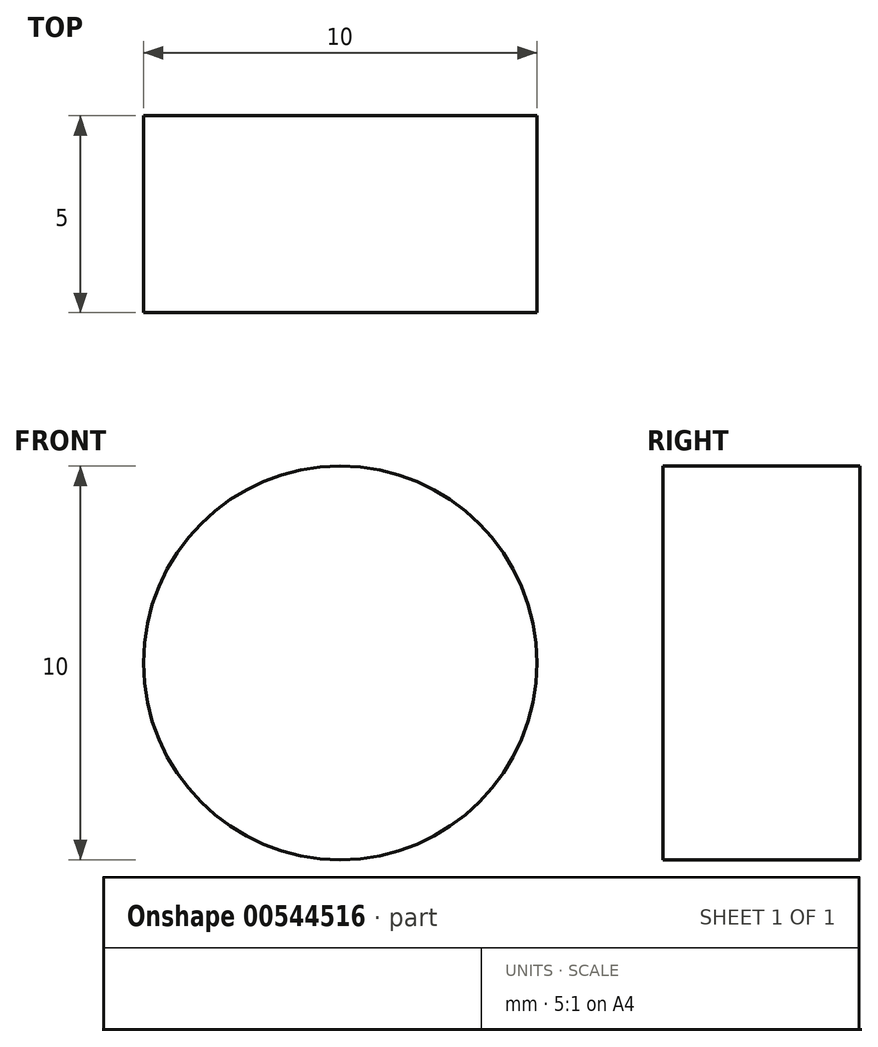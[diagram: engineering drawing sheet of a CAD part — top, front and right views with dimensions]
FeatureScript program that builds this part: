
annotation { "Feature Type Name" : "Feature", "Feature Type Description" : "" }
export const myFeature = defineFeature(function(context is Context, id is Id, definition is map)
    precondition{}
    {
        {
            var Q0;
            Q0=qCreatedBy(makeId("Front.planeOp"),FACE);
            var sketch = newSketch(context, id + "F0", { "sketchPlane" : qUnion([Q0])});
            skLineSegment(sketch, "E0", {"start": v(0, 0) * mm, "end": v(150, 0) * mm});
            skLineSegment(sketch, "E1", {"start": v(150, 0) * mm, "end": v(150, 40) * mm});
            skLineSegment(sketch, "E2", {"start": v(150, 40) * mm, "end": v(0, 40) * mm});
            skLineSegment(sketch, "E3", {"start": v(0, 40) * mm, "end": v(0, 0) * mm});
            skSolve(sketch);
        }
        {
            var Q0;
            Q0=makeQuery(id+"F0.imprint","IMPRINT",FACE,{"disambiguationData":[TD([[makeQuery(id+"F0.imprint","IMPRINT",EDGE,{"derivedFrom":sQuery(id+"F0.wireOp",EDGE,"E0")}),1.0]])]});
            extrude(context, id + "F1", {"entities" : qUnion([Q0]), "depth" : 5 * mm, "offsetDistance" : 25 * mm});
        }
        {
            var Q0;
            Q0=makeQuery(id+"F1.opExtrude","CAP_FACE",FACE,{"disambiguationData":[OSD([sQuery(id+"F0.wireOp",EDGE,"E0"),sQuery(id+"F0.wireOp",EDGE,"E1"),sQuery(id+"F0.wireOp",EDGE,"E2"),sQuery(id+"F0.wireOp",EDGE,"E3")])],"isStart":false});
            var sketch = newSketch(context, id + "F2", { "sketchPlane" : qUnion([Q0])});
            skLineSegment(sketch, "E4", {"start": v(0, 20) * mm, "end": v(15, 20) * mm, "construction": true});
            skPoint(sketch, "E4.endSnap0", {"position": v(0, 20) * mm});
            skLineSegment(sketch, "E5", {"start": v(75, 0) * mm, "end": v(75, 40) * mm, "construction": true});
            skCircle(sketch, "E6", {"center": v(15, 20) * mm, "radius": 5 * mm});
            skCircle(sketch, "E7.MirrorC", {"center": v(135, 20) * mm, "radius": 5 * mm});
            skSolve(sketch);
        }
        {
            var Q0;
            Q0=makeQuery(id+"F2.imprint","IMPRINT",FACE,{"disambiguationData":[TD([[makeQuery(id+"F2.imprint","IMPRINT",EDGE,{"derivedFrom":sQuery(id+"F2.wireOp",EDGE,"E6")}),1.0]])]});
            var Q1;
            Q1=makeQuery(id+"F2.imprint","IMPRINT",FACE,{"disambiguationData":[TD([[makeQuery(id+"F2.imprint","IMPRINT",EDGE,{"derivedFrom":sQuery(id+"F2.wireOp",EDGE,"E7.MirrorC")}),-1.0]])]});
            extrude(context, id + "F3", {"entities" : qUnion([Q0, Q1]), "operationType" : NewBodyOperationType.REMOVE, "endBound" : BoundingType.THROUGH_ALL, "oppositeDirection" : true, "depth" : 25 * mm, "offsetDistance" : 25 * mm});
        }
    });
